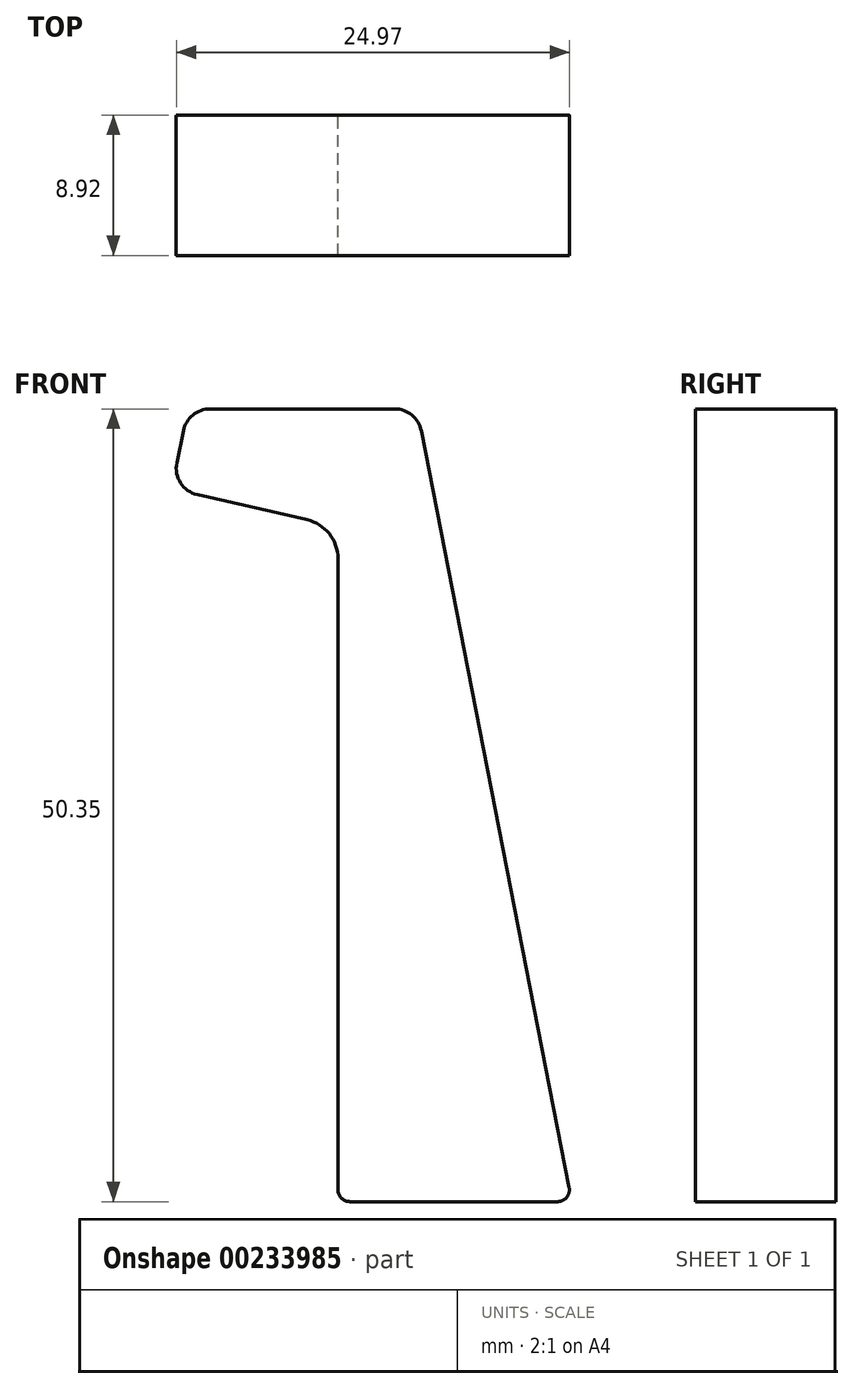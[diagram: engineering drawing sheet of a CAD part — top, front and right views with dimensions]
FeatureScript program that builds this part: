
annotation { "Feature Type Name" : "Feature", "Feature Type Description" : "" }
export const myFeature = defineFeature(function(context is Context, id is Id, definition is map)
    precondition{}
    {
        {
            var Q0;
            Q0=qCreatedBy(makeId("Front.planeOp"),FACE);
            var sketch = newSketch(context, id + "F0", { "sketchPlane" : qUnion([Q0])});
            skLineSegment(sketch, "E0", {"start": v(0, 0.76) * mm, "end": v(0, 40.84) * mm});
            skLineSegment(sketch, "E1", {"start": v(0.76, 0) * mm, "end": v(13.93, 0) * mm});
            skLineSegment(sketch, "E2", {"start": v(14.68, 0.9) * mm, "end": v(5.29, 48.96) * mm});
            skLineSegment(sketch, "E3", {"start": v(3.6, 50.35) * mm, "end": v(-8.13, 50.35) * mm});
            skLineSegment(sketch, "E4", {"start": v(-9.82, 48.97) * mm, "end": v(-10.24, 46.93) * mm});
            skLineSegment(sketch, "E5", {"start": v(-8.93, 44.9) * mm, "end": v(-1.97, 43.31) * mm});
            skPoint(sketch, "E6.visualSharp", {"position": v(0, 42.86) * mm});
            skArc(sketch, "E6.filletArc", {"start": v(0, 40.84) * mm, "mid": v(-0.55, 42.42) * mm, "end": v(-1.97, 43.31) * mm});
            skPoint(sketch, "E7.visualSharp", {"position": v(-10.58, 45.28) * mm});
            skArc(sketch, "E7.filletArc", {"start": v(-10.24, 46.93) * mm, "mid": v(-10, 45.65) * mm, "end": v(-8.93, 44.9) * mm});
            skPoint(sketch, "E8.visualSharp", {"position": v(-9.54, 50.35) * mm});
            skArc(sketch, "E8.filletArc", {"start": v(-8.13, 50.35) * mm, "mid": v(-9.22, 49.97) * mm, "end": v(-9.82, 48.97) * mm});
            skPoint(sketch, "E9.visualSharp", {"position": v(5.02, 50.35) * mm});
            skArc(sketch, "E9.filletArc", {"start": v(5.29, 48.96) * mm, "mid": v(4.7, 49.96) * mm, "end": v(3.6, 50.35) * mm});
            skPoint(sketch, "E10.visualSharp", {"position": v(0, 0) * mm});
            skArc(sketch, "E10.filletArc", {"start": v(0, 0.76) * mm, "mid": v(0.22, 0.22) * mm, "end": v(0.76, 0) * mm});
            skPoint(sketch, "E11.visualSharp", {"position": v(14.86, 0) * mm});
            skArc(sketch, "E11.filletArc", {"start": v(13.93, 0) * mm, "mid": v(14.52, 0.28) * mm, "end": v(14.68, 0.9) * mm});
            skSolve(sketch);
        }
        {
            var Q0;
            Q0=makeQuery(id+"F0.imprint","IMPRINT",FACE,{"disambiguationData":[TD([[makeQuery(id+"F0.imprint","IMPRINT",EDGE,{"derivedFrom":sQuery(id+"F0.wireOp",EDGE,"E0")}),-1.0]])]});
            extrude(context, id + "F1", {"entities" : qUnion([Q0]), "depth" : 8.92 * mm});
        }
    });
